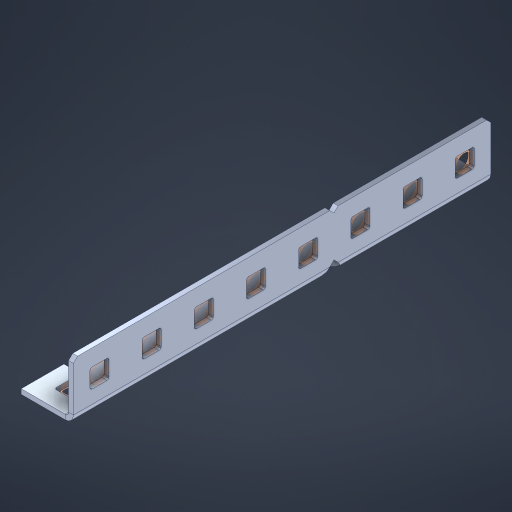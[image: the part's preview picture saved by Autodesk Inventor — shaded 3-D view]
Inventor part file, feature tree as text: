
AUTODESK INVENTOR PART (.ipt)
format: ipt  version: 2023 (Build 270158000, 158)  size: 622,592 bytes
history: native  units: in
note: dims shown in document units (in); Inventor stores cm internally (conversion verified against a paired STEP export)
features: other x31, extrude x22, sheet_metal_op x11, sketch x10, pattern_linear x2, mirror x1, chamfer x1
ambient origin geometry x8: Origin, YZ Plane, XZ Plane, XY Plane, X Axis, Y Axis, Z Axis, Center Point
bodies: Solid1 (feature_tree), Body (feature_tree)
feature tree (78):
  sheet_metal_op  "Flanges"
  other  "Flange Pattern Plane"
  other  "Flange Pattern Sketch"
  sheet_metal_op  "Flange Pattern"
  sheet_metal_op  "Body Pattern"
  pattern_linear  "Center Pattern"  Spacing1=0.0469in  [1 undecoded]
  other  "Arc Length"
  mirror  "Notch Mirror"
  pattern_linear  "Notch Pattern"  Spacing1=0.182in  [1 undecoded]
  chamfer  "End Chamfer"
  extrude  "Half Cut"  Depth=0.02in
  sketch  "Sketch1"  dims[d0=1.0in]
  other  "Plate1"
  sketch  "Sketch2"  dims[d1=4.0in]
  other  "Plate2"
  sheet_metal_op  "Bend1"
  sheet_metal_op  "Corner1"
  sketch  "Sketch3"  dims[d2=0.0469in]
  sketch  "Sketch7"  dims[d3=0.0469in]
  other  "Srf1"
  other  "Srf2"
  sketch  "Sketch8"  dims[d4=0.0234in]
  sketch  "Sketch9"  dims[d5=0.0938in]
  other  "Srf91"
  sheet_metal_op  "Body Pattern Sketch"
  other  "Srf92"
  sketch  "Sketch13"  dims[d6=0.0469in]
  sketch  "Sketch14"  dims[d7=0.5in d8=90.0deg d9=0.0312in]
  sketch  "Sketch15"  dims[d10=0.1875in]
  sketch  "Sketch16"  dims[d11=0.0469in d12=0.0469in d16=0.182in d17=0.02in d18=0.0469in d19=0.0in d20=0.25in d21=0.25in d38=3.1496in d40=0.5in d41=0.3937in d43=1.0in d46=0.172in d47=1.0in d48=0.0in d49=0.182in d50=0.02in d51=0.25in d52=0.25in d53=0.0469in d54=0.0in d55=0.172in d56=1.0in d57=0.0in d58=0.25in d60=3.1496in d62=0.5in d63=0.3937in d65=0.5in d85=0.1227in d86=0.1659in d88=0.04in d89=0.0469in d90=0.0in d91=0.04in d92=0.0491in d95=2.5in d96=0.04in d97=0.25in d98=45.0deg d99=0.25in d100=0.5in d101=0.0in d102=2.497in d106=0.182in d107=0.02in d108=0.5in d109=0.5in d110=0.0469in d111=0.0in d112=0.172in d113=0.5in d114=0.0in d117=0.5in d118=0.5in d119=0.5in]
  other  "Srf786"
  other  "Srf823"
  other  "Srf824"
  other  "Srf825"
  other  "Srf826"
  other  "Srf827"
  other  "Srf828"
  other  "Srf856"
  other  "Srf857"
  other  "Srf858"
  other  "Srf859"
  other  "Srf860"
  other  "Srf861"
  other  "Srf889"
  other  "Srf890"
  other  "Srf891"
  other  "Srf892"
  other  "Srf893"
  other  "Srf894"
  other  "Srf895"
  sheet_metal_op  "Flange Stamp"
  sheet_metal_op  "Flange Circle"
  sheet_metal_op  "Body Stamp"
  sheet_metal_op  "Body Circle"
  other  "Center Stamp"
  other  "Center Circle"
  sheet_metal_op  "Notch"
  extrude  "ExtrusionSrf2"  Depth=0.0469in
  extrude  "ExtrusionSrf92"  TaperAngle=0.0deg  [1 undecoded]
  extrude  "ExtrusionSrf823"  Depth=0.25in
  extrude  "ExtrusionSrf824"  Depth=0.25in
  extrude  "ExtrusionSrf825"  Depth=0.5in
  extrude  "ExtrusionSrf826"  Depth=0.5in
  extrude  "ExtrusionSrf827"  Depth=1.0in TaperAngle=0.0deg
  extrude  "ExtrusionSrf828"  Depth=0.182in
  extrude  "ExtrusionSrf856"  Depth=0.02in
  extrude  "ExtrusionSrf857"  Depth=0.25in
  extrude  "ExtrusionSrf858"  Depth=0.25in
  extrude  "ExtrusionSrf859"  Depth=0.0469in
  extrude  "ExtrusionSrf860"  TaperAngle=0.0deg  [1 undecoded]
  extrude  "ExtrusionSrf861"  Depth=0.5in
  extrude  "ExtrusionSrf889"  Depth=1.0in TaperAngle=0.0deg
  extrude  "ExtrusionSrf890"  Depth=0.25in
  extrude  "ExtrusionSrf891"  Depth=0.5in
  extrude  "ExtrusionSrf892"  Depth=0.5in
  extrude  "ExtrusionSrf893"  Depth=0.5in
  extrude  "ExtrusionSrf894"  Depth=0.5in
  extrude  "ExtrusionSrf895"  Depth=0.5in
note: 4 required parameter values undecoded (feature->parameter linkage not recoverable at this tier; creation-order binding heuristic only, values carry confidence <= 0.55)
